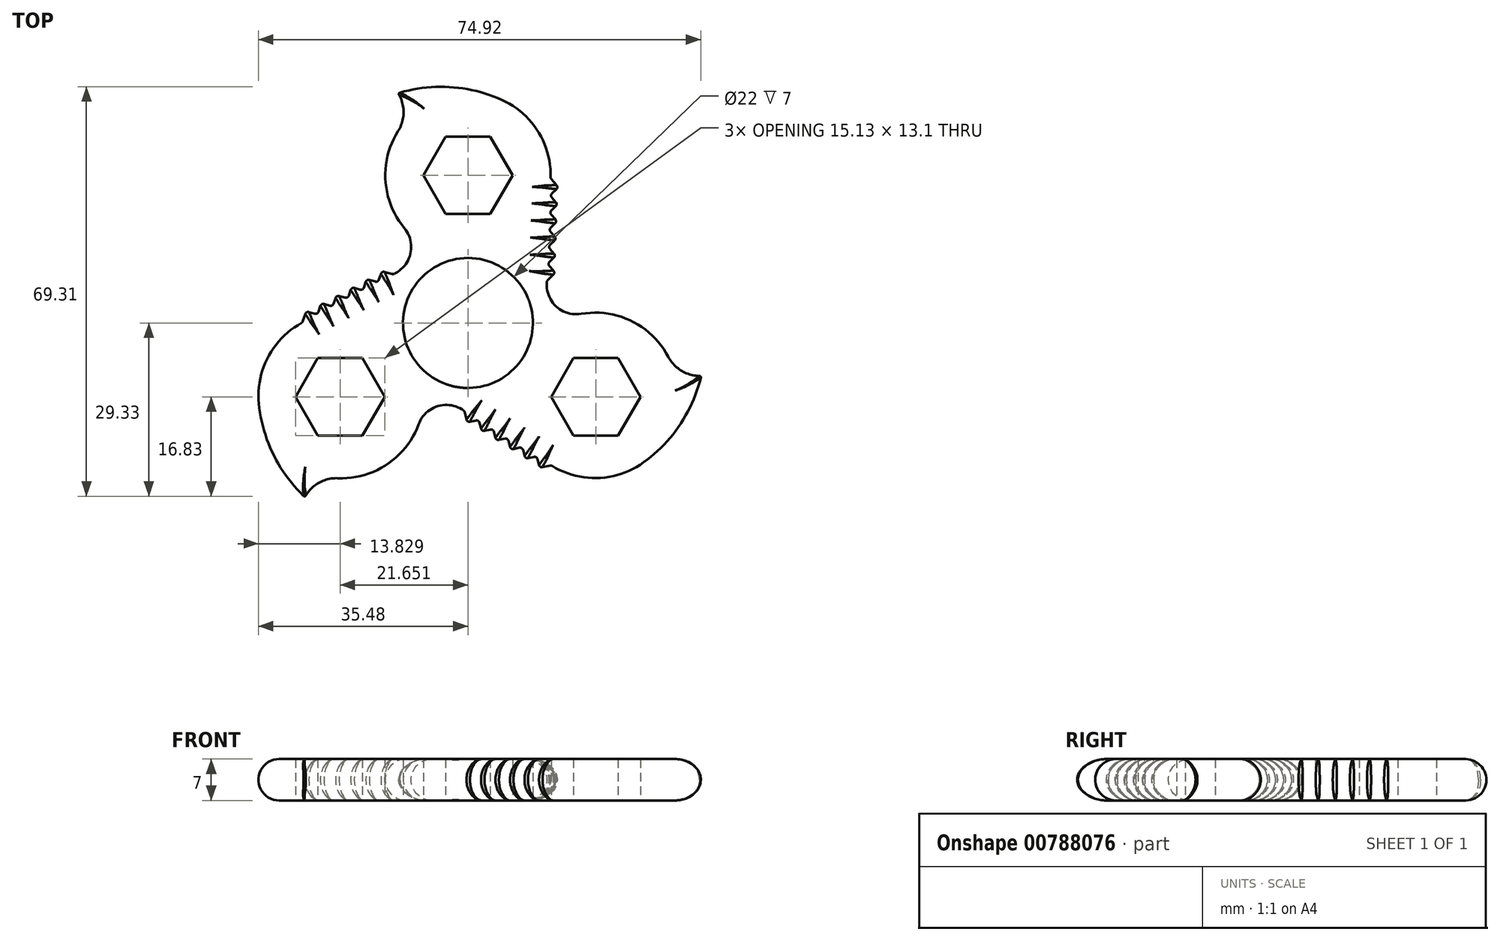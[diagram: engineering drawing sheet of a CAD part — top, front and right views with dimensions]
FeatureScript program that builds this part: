
annotation { "Feature Type Name" : "Feature", "Feature Type Description" : "" }
export const myFeature = defineFeature(function(context is Context, id is Id, definition is map)
    precondition{}
    {
        {
            var Q0;
            Q0=qCreatedBy(makeId("Top.planeOp"),FACE);
            var sketch = newSketch(context, id + "F0", { "sketchPlane" : qUnion([Q0])});
            skCircle(sketch, "E0", {"center": v(0, 0) * mm, "radius": 39 * mm, "construction": true});
            skCircle(sketch, "E1", {"center": v(0, 0) * mm, "radius": 11 * mm});
            skPoint(sketch, "E2.center", {"position": v(0.03, 0) * mm});
            skArc(sketch, "E3", {"start": v(14, 24.5) * mm, "mid": v(11.9, 32.39) * mm, "end": v(5.75, 37.77) * mm});
            skLineSegment(sketch, "E4", {"start": v(13.35, 6.66) * mm, "end": v(13.36, 7.1) * mm});
            skPoint(sketch, "E5.visualSharp", {"position": v(-4.7, 11.81) * mm});
            skArc(sketch, "E5.filletArc", {"start": v(-12.27, 8.44) * mm, "mid": v(-9.7, 11.89) * mm, "end": v(-10.77, 16.05) * mm});
            skPoint(sketch, "E6.visualSharp", {"position": v(13.05, -1.63) * mm});
            skArc(sketch, "E7", {"start": v(5.75, 37.77) * mm, "mid": v(-2.94, 39.93) * mm, "end": v(-11.83, 38.9) * mm});
            skArc(sketch, "E8", {"start": v(-11.83, 32.48) * mm, "mid": v(-10.9, 35.7) * mm, "end": v(-11.83, 38.9) * mm});
            skArc(sketch, "E9.trimOffspring", {"start": v(-11.83, 32.48) * mm, "mid": v(-13.97, 24.1) * mm, "end": v(-10.77, 16.05) * mm});
            skLineSegment(sketch, "E10", {"start": v(14, 24.5) * mm, "end": v(15.31, 23) * mm});
            skLineSegment(sketch, "E11", {"start": v(15.31, 23) * mm, "end": v(13.89, 21.6) * mm});
            skLineSegment(sketch, "E12.1.0.0", {"start": v(15.2, 20.1) * mm, "end": v(13.78, 18.7) * mm});
            skLineSegment(sketch, "E12.1.0.1", {"start": v(13.89, 21.6) * mm, "end": v(15.2, 20.1) * mm});
            skLineSegment(sketch, "E12.2.0.0", {"start": v(15.1, 17.2) * mm, "end": v(13.68, 15.8) * mm});
            skLineSegment(sketch, "E12.2.0.1", {"start": v(13.78, 18.7) * mm, "end": v(15.1, 17.2) * mm});
            skLineSegment(sketch, "E12.3.0.0", {"start": v(15, 14.3) * mm, "end": v(13.57, 12.9) * mm});
            skLineSegment(sketch, "E12.3.0.1", {"start": v(13.68, 15.8) * mm, "end": v(15, 14.3) * mm});
            skLineSegment(sketch, "E12.4.0.0", {"start": v(14.9, 11.4) * mm, "end": v(13.47, 10) * mm});
            skLineSegment(sketch, "E12.4.0.1", {"start": v(13.57, 12.9) * mm, "end": v(14.9, 11.4) * mm});
            skLineSegment(sketch, "E12.5.0.0", {"start": v(14.79, 8.5) * mm, "end": v(13.36, 7.1) * mm});
            skLineSegment(sketch, "E12.5.0.1", {"start": v(13.47, 10) * mm, "end": v(14.79, 8.5) * mm});
            skArc(sketch, "E13.1.0", {"start": v(-22.04, -26.28) * mm, "mid": v(-25.29, -27.08) * mm, "end": v(-27.6, -29.49) * mm});
            skArc(sketch, "E13.1.1", {"start": v(-1, -14.64) * mm, "mid": v(-5.27, -14.14) * mm, "end": v(-8.35, -17.14) * mm});
            skArc(sketch, "E13.1.2", {"start": v(-22.04, -26.28) * mm, "mid": v(-13.71, -23.93) * mm, "end": v(-8.35, -17.14) * mm});
            skArc(sketch, "E13.1.3", {"start": v(-35.41, -13.7) * mm, "mid": v(-32.94, -22.3) * mm, "end": v(-27.6, -29.49) * mm});
            skArc(sketch, "E13.1.4", {"start": v(-28.04, 0.08) * mm, "mid": v(-33.82, -5.68) * mm, "end": v(-35.41, -13.7) * mm});
            skLineSegment(sketch, "E13.1.6", {"start": v(-28.04, 0.08) * mm, "end": v(-27.4, 1.98) * mm});
            skLineSegment(sketch, "E13.1.7", {"start": v(-27.4, 1.98) * mm, "end": v(-25.47, 1.44) * mm});
            skLineSegment(sketch, "E13.1.8", {"start": v(-25.48, 1.44) * mm, "end": v(-24.84, 3.34) * mm});
            skLineSegment(sketch, "E13.1.9", {"start": v(-24.84, 3.34) * mm, "end": v(-22.91, 2.8) * mm});
            skLineSegment(sketch, "E13.1.10", {"start": v(-22.91, 2.8) * mm, "end": v(-22.28, 4.7) * mm});
            skLineSegment(sketch, "E13.1.11", {"start": v(-22.28, 4.7) * mm, "end": v(-20.35, 4.16) * mm});
            skLineSegment(sketch, "E13.1.12", {"start": v(-20.35, 4.16) * mm, "end": v(-19.71, 6.05) * mm});
            skLineSegment(sketch, "E13.1.13", {"start": v(-19.71, 6.05) * mm, "end": v(-17.79, 5.52) * mm});
            skLineSegment(sketch, "E13.1.14", {"start": v(-17.79, 5.51) * mm, "end": v(-17.15, 7.41) * mm});
            skLineSegment(sketch, "E13.1.15", {"start": v(-17.15, 7.41) * mm, "end": v(-15.23, 6.87) * mm});
            skLineSegment(sketch, "E13.1.16", {"start": v(-15.23, 6.87) * mm, "end": v(-14.59, 8.77) * mm});
            skLineSegment(sketch, "E13.1.17", {"start": v(-14.59, 8.77) * mm, "end": v(-12.66, 8.23) * mm});
            skLineSegment(sketch, "E13.1.18", {"start": v(-12.27, 8.44) * mm, "end": v(-12.66, 8.23) * mm});
            skArc(sketch, "E13.2.0", {"start": v(33.95, -5.74) * mm, "mid": v(36.26, -8.15) * mm, "end": v(39.5, -8.95) * mm});
            skArc(sketch, "E13.2.1", {"start": v(13.35, 6.66) * mm, "mid": v(15.05, 2.72) * mm, "end": v(19.19, 1.55) * mm});
            skArc(sketch, "E13.2.2", {"start": v(33.95, -5.74) * mm, "mid": v(27.75, 0.3) * mm, "end": v(19.19, 1.55) * mm});
            skArc(sketch, "E13.2.3", {"start": v(29.73, -23.6) * mm, "mid": v(35.95, -17.16) * mm, "end": v(39.5, -8.95) * mm});
            skArc(sketch, "E13.2.4", {"start": v(14.12, -24.11) * mm, "mid": v(22, -26.24) * mm, "end": v(29.73, -23.6) * mm});
            skLineSegment(sketch, "E13.2.6", {"start": v(14.12, -24.11) * mm, "end": v(12.16, -24.5) * mm});
            skLineSegment(sketch, "E13.2.7", {"start": v(12.16, -24.5) * mm, "end": v(11.66, -22.57) * mm});
            skLineSegment(sketch, "E13.2.8", {"start": v(11.66, -22.57) * mm, "end": v(9.7, -22.97) * mm});
            skLineSegment(sketch, "E13.2.9", {"start": v(9.7, -22.97) * mm, "end": v(9.2, -21.03) * mm});
            skLineSegment(sketch, "E13.2.10", {"start": v(9.2, -21.03) * mm, "end": v(7.24, -21.43) * mm});
            skLineSegment(sketch, "E13.2.11", {"start": v(7.24, -21.43) * mm, "end": v(6.74, -19.5) * mm});
            skLineSegment(sketch, "E13.2.12", {"start": v(6.75, -19.5) * mm, "end": v(4.79, -19.89) * mm});
            skLineSegment(sketch, "E13.2.13", {"start": v(4.79, -19.89) * mm, "end": v(4.29, -17.95) * mm});
            skLineSegment(sketch, "E13.2.14", {"start": v(4.29, -17.95) * mm, "end": v(2.33, -18.35) * mm});
            skLineSegment(sketch, "E13.2.15", {"start": v(2.33, -18.35) * mm, "end": v(1.83, -16.41) * mm});
            skLineSegment(sketch, "E13.2.16", {"start": v(1.83, -16.41) * mm, "end": v(-0.13, -16.8) * mm});
            skLineSegment(sketch, "E13.2.17", {"start": v(-0.13, -16.8) * mm, "end": v(-0.63, -14.87) * mm});
            skLineSegment(sketch, "E13.2.18", {"start": v(-1, -14.64) * mm, "end": v(-0.63, -14.87) * mm});
            skPoint(sketch, "E13.center", {"position": v(0.02, 0.15) * mm});
            skLineSegment(sketch, "E14.trimOffspring", {"start": v(-25.47, 1.44) * mm, "end": v(-25.48, 1.44) * mm});
            skLineSegment(sketch, "E15.trimOffspring", {"start": v(-22.91, 2.8) * mm, "end": v(-22.91, 2.8) * mm});
            skLineSegment(sketch, "E16.trimOffspring", {"start": v(-20.35, 4.16) * mm, "end": v(-20.35, 4.16) * mm});
            skLineSegment(sketch, "E17.trimOffspring", {"start": v(-17.79, 5.52) * mm, "end": v(-17.79, 5.51) * mm});
            skLineSegment(sketch, "E18.trimOffspring", {"start": v(-15.23, 6.87) * mm, "end": v(-15.23, 6.87) * mm});
            skLineSegment(sketch, "E19.trimOffspring", {"start": v(1.83, -16.41) * mm, "end": v(1.83, -16.41) * mm});
            skLineSegment(sketch, "E20.trimOffspring", {"start": v(4.29, -17.95) * mm, "end": v(4.29, -17.95) * mm});
            skLineSegment(sketch, "E21.trimOffspring", {"start": v(6.74, -19.5) * mm, "end": v(6.75, -19.5) * mm});
            skLineSegment(sketch, "E22.trimOffspring", {"start": v(9.2, -21.03) * mm, "end": v(9.2, -21.03) * mm});
            skLineSegment(sketch, "E23.trimOffspring", {"start": v(11.26, -22.32) * mm, "end": v(11.66, -22.57) * mm});
            skLineSegment(sketch, "E24.trimOffspring", {"start": v(13.47, 10) * mm, "end": v(13.47, 10) * mm});
            skLineSegment(sketch, "E25.trimOffspring", {"start": v(13.57, 12.9) * mm, "end": v(13.57, 12.9) * mm});
            skLineSegment(sketch, "E26.trimOffspring", {"start": v(13.68, 15.8) * mm, "end": v(13.68, 15.8) * mm});
            skLineSegment(sketch, "E27.trimOffspring", {"start": v(13.78, 18.7) * mm, "end": v(13.78, 18.7) * mm});
            skLineSegment(sketch, "E28.trimOffspring", {"start": v(13.78, 18.7) * mm, "end": v(13.78, 18.7) * mm, "construction": true});
            skLineSegment(sketch, "E29.trimOffspring", {"start": v(13.89, 21.6) * mm, "end": v(13.89, 21.6) * mm});
            skCircle(sketch, "E30.cCircle", {"center": v(0, 25) * mm, "radius": 6.55 * mm, "construction": true});
            skLineSegment(sketch, "E30.0", {"start": v(7.56, 25) * mm, "end": v(3.78, 18.45) * mm});
            skLineSegment(sketch, "E30.1", {"start": v(3.78, 18.45) * mm, "end": v(-3.78, 18.45) * mm});
            skLineSegment(sketch, "E30.2", {"start": v(-3.78, 18.45) * mm, "end": v(-7.56, 25) * mm});
            skLineSegment(sketch, "E30.3", {"start": v(-7.56, 25) * mm, "end": v(-3.78, 31.55) * mm});
            skLineSegment(sketch, "E30.4", {"start": v(-3.78, 31.55) * mm, "end": v(3.78, 31.55) * mm});
            skLineSegment(sketch, "E30.5", {"start": v(3.78, 31.55) * mm, "end": v(7.56, 25) * mm});
            skPoint(sketch, "E30.0.midPoint", {"position": v(5.67, 21.72) * mm});
            skLineSegment(sketch, "E31.1.0", {"start": v(-25.43, -19.05) * mm, "end": v(-29.21, -12.5) * mm});
            skPoint(sketch, "E31.1.1", {"position": v(-21.65, -5.95) * mm});
            skLineSegment(sketch, "E31.1.2", {"start": v(-17.87, -19.05) * mm, "end": v(-25.43, -19.05) * mm});
            skLineSegment(sketch, "E31.1.3", {"start": v(-14.09, -12.5) * mm, "end": v(-17.87, -19.05) * mm});
            skLineSegment(sketch, "E31.1.4", {"start": v(-17.87, -5.95) * mm, "end": v(-14.09, -12.5) * mm});
            skLineSegment(sketch, "E31.1.5", {"start": v(-29.21, -12.5) * mm, "end": v(-25.43, -5.95) * mm});
            skCircle(sketch, "E31.1.6", {"center": v(-21.65, -12.5) * mm, "radius": 6.55 * mm, "construction": true});
            skLineSegment(sketch, "E31.1.7", {"start": v(-25.43, -5.95) * mm, "end": v(-17.87, -5.95) * mm});
            skLineSegment(sketch, "E31.2.0", {"start": v(29.21, -12.5) * mm, "end": v(25.43, -19.05) * mm});
            skPoint(sketch, "E31.2.1", {"position": v(15.98, -15.77) * mm});
            skLineSegment(sketch, "E31.2.2", {"start": v(25.43, -5.95) * mm, "end": v(29.21, -12.5) * mm});
            skLineSegment(sketch, "E31.2.3", {"start": v(17.87, -5.95) * mm, "end": v(25.43, -5.95) * mm});
            skLineSegment(sketch, "E31.2.4", {"start": v(14.09, -12.5) * mm, "end": v(17.87, -5.95) * mm});
            skLineSegment(sketch, "E31.2.5", {"start": v(25.43, -19.05) * mm, "end": v(17.87, -19.05) * mm});
            skCircle(sketch, "E31.2.6", {"center": v(21.65, -12.5) * mm, "radius": 6.55 * mm, "construction": true});
            skLineSegment(sketch, "E31.2.7", {"start": v(17.87, -19.05) * mm, "end": v(14.09, -12.5) * mm});
            skSolve(sketch);
        }
        {
            var Q0;
            Q0=qSketchRegion(id+"F0",true);
            extrude(context, id + "F1", {"entities" : qUnion([Q0]), "depth" : 7 * mm, "offsetDistance" : 25 * mm});
        }
        {
            var Q0;
            Q0=makeQuery(id+"F1.opExtrude","SWEPT_EDGE",EDGE,{"disambiguationData":[OSD([sQuery(id+"F0.wireOp",EDGE,"E13.1.17"),sQuery(id+"F0.wireOp",EDGE,"E13.1.18")])]});
            var Q1;
            Q1=makeQuery(id+"F1.opExtrude","SWEPT_EDGE",EDGE,{"disambiguationData":[OSD([sQuery(id+"F0.wireOp",EDGE,"E13.1.16"),sQuery(id+"F0.wireOp",EDGE,"E13.1.17")])]});
            var Q2;
            Q2=makeQuery(id+"F1.opExtrude","SWEPT_EDGE",EDGE,{"disambiguationData":[OSD([sQuery(id+"F0.wireOp",EDGE,"E13.1.15"),sQuery(id+"F0.wireOp",EDGE,"E13.1.16")])]});
            var Q3;
            Q3=makeQuery(id+"F1.opExtrude","SWEPT_EDGE",EDGE,{"disambiguationData":[OSD([sQuery(id+"F0.wireOp",EDGE,"E13.1.14"),sQuery(id+"F0.wireOp",EDGE,"E13.1.15")])]});
            var Q4;
            Q4=makeQuery(id+"F1.opExtrude","SWEPT_EDGE",EDGE,{"disambiguationData":[OSD([sQuery(id+"F0.wireOp",EDGE,"E13.1.13"),sQuery(id+"F0.wireOp",EDGE,"E13.1.14")])]});
            var Q5;
            Q5=makeQuery(id+"F1.opExtrude","SWEPT_EDGE",EDGE,{"disambiguationData":[OSD([sQuery(id+"F0.wireOp",EDGE,"E13.1.12"),sQuery(id+"F0.wireOp",EDGE,"E13.1.13")])]});
            var Q6;
            Q6=makeQuery(id+"F1.opExtrude","SWEPT_EDGE",EDGE,{"disambiguationData":[OSD([sQuery(id+"F0.wireOp",EDGE,"E13.1.11"),sQuery(id+"F0.wireOp",EDGE,"E13.1.12")])]});
            var Q7;
            Q7=makeQuery(id+"F1.opExtrude","SWEPT_EDGE",EDGE,{"disambiguationData":[OSD([sQuery(id+"F0.wireOp",EDGE,"E13.1.10"),sQuery(id+"F0.wireOp",EDGE,"E13.1.11")])]});
            var Q8;
            Q8=makeQuery(id+"F1.opExtrude","SWEPT_EDGE",EDGE,{"disambiguationData":[OSD([sQuery(id+"F0.wireOp",EDGE,"E13.1.9"),sQuery(id+"F0.wireOp",EDGE,"E13.1.10")])]});
            var Q9;
            Q9=makeQuery(id+"F1.opExtrude","SWEPT_EDGE",EDGE,{"disambiguationData":[OSD([sQuery(id+"F0.wireOp",EDGE,"E13.1.8"),sQuery(id+"F0.wireOp",EDGE,"E13.1.9")])]});
            var Q10;
            Q10=makeQuery(id+"F1.opExtrude","SWEPT_EDGE",EDGE,{"disambiguationData":[OSD([sQuery(id+"F0.wireOp",EDGE,"E13.1.7"),sQuery(id+"F0.wireOp",EDGE,"E13.1.8")])]});
            var Q11;
            Q11=makeQuery(id+"F1.opExtrude","SWEPT_EDGE",EDGE,{"disambiguationData":[OSD([sQuery(id+"F0.wireOp",EDGE,"E13.1.6"),sQuery(id+"F0.wireOp",EDGE,"E13.1.7")])]});
            var Q12;
            Q12=makeQuery(id+"F1.opExtrude","SWEPT_EDGE",EDGE,{"disambiguationData":[OSD([sQuery(id+"F0.wireOp",EDGE,"E13.1.4"),sQuery(id+"F0.wireOp",EDGE,"E13.1.6")])]});
            var Q13;
            Q13=makeQuery(id+"F1.opExtrude","SWEPT_EDGE",EDGE,{"disambiguationData":[OSD([sQuery(id+"F0.wireOp",EDGE,"E13.2.17"),sQuery(id+"F0.wireOp",EDGE,"E13.2.18")])]});
            var Q14;
            Q14=makeQuery(id+"F1.opExtrude","SWEPT_EDGE",EDGE,{"disambiguationData":[OSD([sQuery(id+"F0.wireOp",EDGE,"E13.2.16"),sQuery(id+"F0.wireOp",EDGE,"E13.2.17")])]});
            var Q15;
            Q15=makeQuery(id+"F1.opExtrude","SWEPT_EDGE",EDGE,{"disambiguationData":[OSD([sQuery(id+"F0.wireOp",EDGE,"E13.2.15"),sQuery(id+"F0.wireOp",EDGE,"E13.2.16")])]});
            var Q16;
            Q16=makeQuery(id+"F1.opExtrude","SWEPT_EDGE",EDGE,{"disambiguationData":[OSD([sQuery(id+"F0.wireOp",EDGE,"E13.2.14"),sQuery(id+"F0.wireOp",EDGE,"E13.2.15")])]});
            var Q17;
            Q17=makeQuery(id+"F1.opExtrude","SWEPT_EDGE",EDGE,{"disambiguationData":[OSD([sQuery(id+"F0.wireOp",EDGE,"E13.2.13"),sQuery(id+"F0.wireOp",EDGE,"E13.2.14")])]});
            var Q18;
            Q18=makeQuery(id+"F1.opExtrude","SWEPT_EDGE",EDGE,{"disambiguationData":[OSD([sQuery(id+"F0.wireOp",EDGE,"E13.2.12"),sQuery(id+"F0.wireOp",EDGE,"E13.2.13")])]});
            var Q19;
            Q19=makeQuery(id+"F1.opExtrude","SWEPT_EDGE",EDGE,{"disambiguationData":[OSD([sQuery(id+"F0.wireOp",EDGE,"E13.2.11"),sQuery(id+"F0.wireOp",EDGE,"E13.2.12")])]});
            var Q20;
            Q20=makeQuery(id+"F1.opExtrude","SWEPT_EDGE",EDGE,{"disambiguationData":[OSD([sQuery(id+"F0.wireOp",EDGE,"E13.2.10"),sQuery(id+"F0.wireOp",EDGE,"E13.2.11")])]});
            var Q21;
            Q21=makeQuery(id+"F1.opExtrude","SWEPT_EDGE",EDGE,{"disambiguationData":[OSD([sQuery(id+"F0.wireOp",EDGE,"E13.2.9"),sQuery(id+"F0.wireOp",EDGE,"E13.2.10")])]});
            var Q22;
            Q22=makeQuery(id+"F1.opExtrude","SWEPT_EDGE",EDGE,{"disambiguationData":[OSD([sQuery(id+"F0.wireOp",EDGE,"E13.2.8"),sQuery(id+"F0.wireOp",EDGE,"E13.2.9")])]});
            var Q23;
            Q23=makeQuery(id+"F1.opExtrude","SWEPT_EDGE",EDGE,{"disambiguationData":[OSD([sQuery(id+"F0.wireOp",EDGE,"E13.2.7"),sQuery(id+"F0.wireOp",EDGE,"E13.2.8")])]});
            var Q24;
            Q24=makeQuery(id+"F1.opExtrude","SWEPT_EDGE",EDGE,{"disambiguationData":[OSD([sQuery(id+"F0.wireOp",EDGE,"E13.2.6"),sQuery(id+"F0.wireOp",EDGE,"E13.2.7")])]});
            var Q25;
            Q25=makeQuery(id+"F1.opExtrude","SWEPT_EDGE",EDGE,{"disambiguationData":[OSD([sQuery(id+"F0.wireOp",EDGE,"E13.2.4"),sQuery(id+"F0.wireOp",EDGE,"E13.2.6")])]});
            var Q26;
            Q26=makeQuery(id+"F1.opExtrude","SWEPT_EDGE",EDGE,{"disambiguationData":[OSD([sQuery(id+"F0.wireOp",EDGE,"E3"),sQuery(id+"F0.wireOp",EDGE,"E10")])]});
            var Q27;
            Q27=makeQuery(id+"F1.opExtrude","SWEPT_EDGE",EDGE,{"disambiguationData":[OSD([sQuery(id+"F0.wireOp",EDGE,"E10"),sQuery(id+"F0.wireOp",EDGE,"E11")])]});
            var Q28;
            Q28=makeQuery(id+"F1.opExtrude","SWEPT_EDGE",EDGE,{"disambiguationData":[OSD([sQuery(id+"F0.wireOp",EDGE,"E11"),sQuery(id+"F0.wireOp",EDGE,"E12.1.0.1")])]});
            var Q29;
            Q29=makeQuery(id+"F1.opExtrude","SWEPT_EDGE",EDGE,{"disambiguationData":[OSD([sQuery(id+"F0.wireOp",EDGE,"E12.1.0.0"),sQuery(id+"F0.wireOp",EDGE,"E12.1.0.1")])]});
            var Q30;
            Q30=makeQuery(id+"F1.opExtrude","SWEPT_EDGE",EDGE,{"disambiguationData":[OSD([sQuery(id+"F0.wireOp",EDGE,"E12.1.0.0"),sQuery(id+"F0.wireOp",EDGE,"E12.2.0.1")])]});
            var Q31;
            Q31=makeQuery(id+"F1.opExtrude","SWEPT_EDGE",EDGE,{"disambiguationData":[OSD([sQuery(id+"F0.wireOp",EDGE,"E12.2.0.0"),sQuery(id+"F0.wireOp",EDGE,"E12.2.0.1")])]});
            var Q32;
            Q32=makeQuery(id+"F1.opExtrude","SWEPT_EDGE",EDGE,{"disambiguationData":[OSD([sQuery(id+"F0.wireOp",EDGE,"E12.2.0.0"),sQuery(id+"F0.wireOp",EDGE,"E12.3.0.1")])]});
            var Q33;
            Q33=makeQuery(id+"F1.opExtrude","SWEPT_EDGE",EDGE,{"disambiguationData":[OSD([sQuery(id+"F0.wireOp",EDGE,"E12.3.0.0"),sQuery(id+"F0.wireOp",EDGE,"E12.3.0.1")])]});
            var Q34;
            Q34=makeQuery(id+"F1.opExtrude","SWEPT_EDGE",EDGE,{"disambiguationData":[OSD([sQuery(id+"F0.wireOp",EDGE,"E12.3.0.0"),sQuery(id+"F0.wireOp",EDGE,"E12.4.0.1")])]});
            var Q35;
            Q35=makeQuery(id+"F1.opExtrude","SWEPT_EDGE",EDGE,{"disambiguationData":[OSD([sQuery(id+"F0.wireOp",EDGE,"E12.4.0.0"),sQuery(id+"F0.wireOp",EDGE,"E12.4.0.1")])]});
            var Q36;
            Q36=makeQuery(id+"F1.opExtrude","SWEPT_EDGE",EDGE,{"disambiguationData":[OSD([sQuery(id+"F0.wireOp",EDGE,"E12.4.0.0"),sQuery(id+"F0.wireOp",EDGE,"E12.5.0.1")])]});
            var Q37;
            Q37=makeQuery(id+"F1.opExtrude","SWEPT_EDGE",EDGE,{"disambiguationData":[OSD([sQuery(id+"F0.wireOp",EDGE,"E12.5.0.0"),sQuery(id+"F0.wireOp",EDGE,"E12.5.0.1")])]});
            var Q38;
            Q38=makeQuery(id+"F1.opExtrude","SWEPT_EDGE",EDGE,{"disambiguationData":[OSD([sQuery(id+"F0.wireOp",EDGE,"E4"),sQuery(id+"F0.wireOp",EDGE,"E12.5.0.0")])]});
            fillet(context, id + "F2", {"entities" : qUnion([Q0, Q1, Q2, Q3, Q4, Q5, Q6, Q7, Q8, Q9, Q10, Q11, Q12, Q13, Q14, Q15, Q16, Q17, Q18, Q19, Q20, Q21, Q22, Q23, Q24, Q25, Q26, Q27, Q28, Q29, Q30, Q31, Q32, Q33, Q34, Q35, Q36, Q37, Q38]), "radius" : .5 * mm, "tangentPropagation" : true, "allowEdgeOverflow" : false});
        }
        {
            var Q0;
            Q0=makeQuery(id+"F1.opExtrude","SWEPT_EDGE",EDGE,{"disambiguationData":[OSD([sQuery(id+"F0.wireOp",EDGE,"E7"),sQuery(id+"F0.wireOp",EDGE,"E8")])]});
            var Q1;
            Q1=makeQuery(id+"F1.opExtrude","SWEPT_EDGE",EDGE,{"disambiguationData":[OSD([sQuery(id+"F0.wireOp",EDGE,"E13.1.0"),sQuery(id+"F0.wireOp",EDGE,"E13.1.3")])]});
            var Q2;
            Q2=makeQuery(id+"F1.opExtrude","SWEPT_EDGE",EDGE,{"disambiguationData":[OSD([sQuery(id+"F0.wireOp",EDGE,"E13.2.0"),sQuery(id+"F0.wireOp",EDGE,"E13.2.3")])]});
            fillet(context, id + "F3", {"entities" : qUnion([Q0, Q1, Q2]), "radius" : .25 * mm, "tangentPropagation" : true, "allowEdgeOverflow" : false});
        }
        {
            var Q0;
            Q0=makeQuery(id+"F1.opExtrude","CAP_EDGE",EDGE,{"disambiguationData":[OSD([sQuery(id+"F0.wireOp",EDGE,"E13.2.4")])],"isStart":false});
            var Q1;
            Q1=makeQuery(id+"F1.opExtrude","CAP_EDGE",EDGE,{"disambiguationData":[OSD([sQuery(id+"F0.wireOp",EDGE,"E13.1.1")])],"isStart":true});
            fillet(context, id + "F4", {"entities" : qUnion([Q0, Q1]), "radius" : 3.5 * mm, "tangentPropagation" : true, "allowEdgeOverflow" : false});
        }
    });
